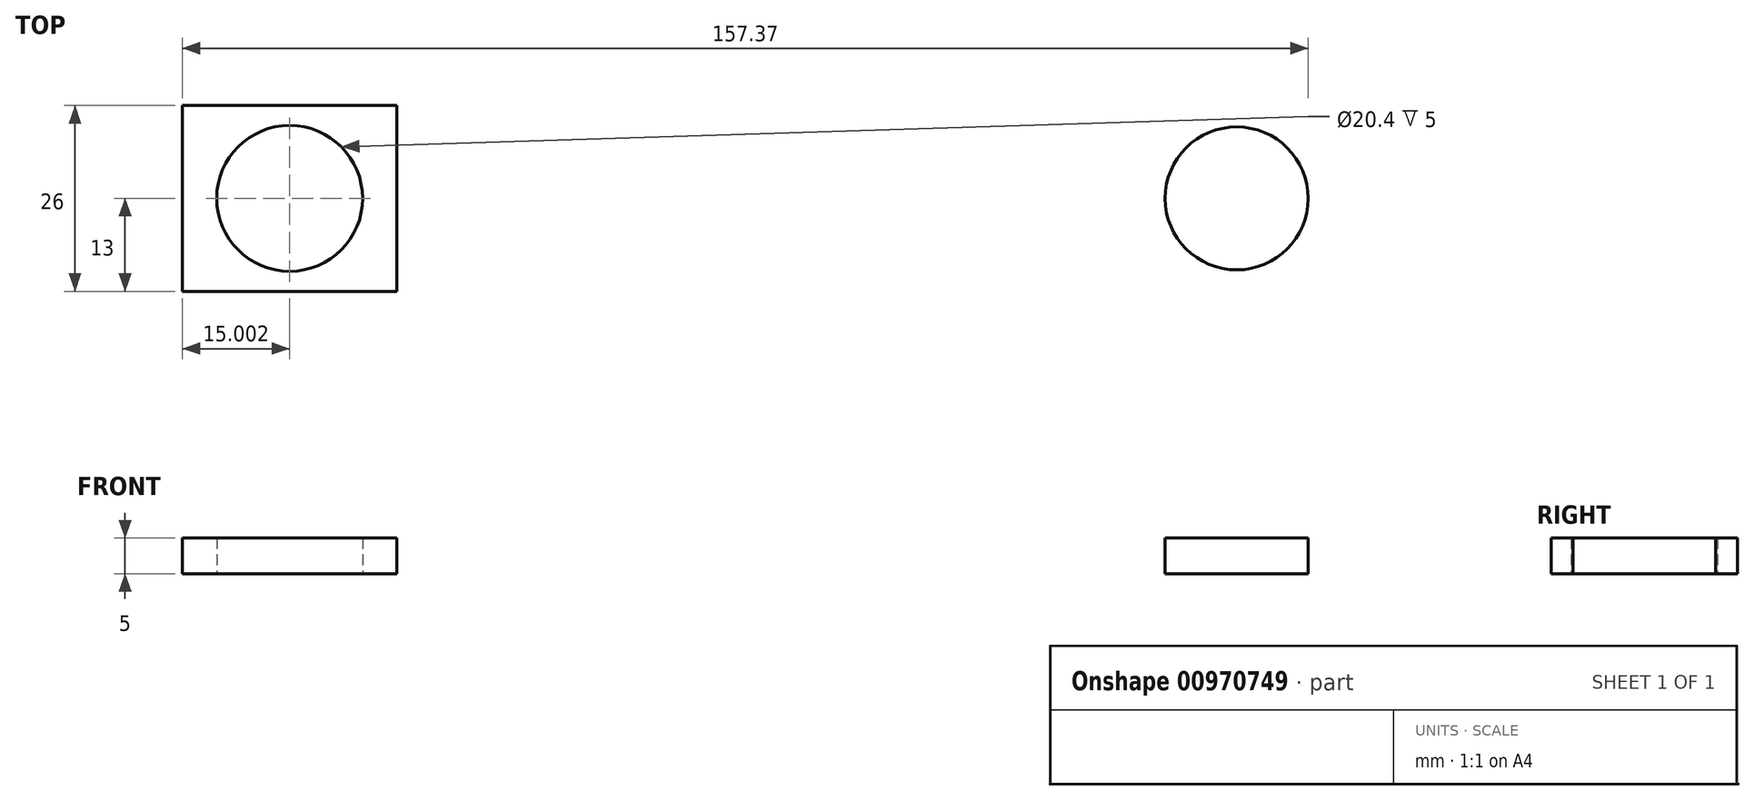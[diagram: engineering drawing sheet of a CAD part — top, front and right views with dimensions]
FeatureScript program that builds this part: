
annotation { "Feature Type Name" : "Feature", "Feature Type Description" : "" }
export const myFeature = defineFeature(function(context is Context, id is Id, definition is map)
    precondition{}
    {
        {
            var Q0;
            Q0=qCreatedBy(makeId("Top.planeOp"),FACE);
            var sketch = newSketch(context, id + "F0", { "sketchPlane" : qUnion([Q0])});
            skLineSegment(sketch, "E0", {"start": v(-147.37, -13) * mm, "end": v(-147.37, 13) * mm});
            skPoint(sketch, "E1.centerSnap0", {"position": v(-147.37, 0) * mm});
            skPoint(sketch, "E2", {"position": v(-143.37, 9) * mm});
            skPoint(sketch, "E3", {"position": v(-143.37, -9) * mm});
            skLineSegment(sketch, "E4", {"start": v(-117.37, 13) * mm, "end": v(-117.37, -13) * mm});
            skCircle(sketch, "E5", {"center": v(-132.37, 0) * mm, "radius": 10.2 * mm});
            skLineSegment(sketch, "E6", {"start": v(-147.37, 13) * mm, "end": v(-117.37, 13) * mm});
            skLineSegment(sketch, "E7", {"start": v(-147.37, -13) * mm, "end": v(-117.37, -13) * mm});
            skPoint(sketch, "E8", {"position": v(-121.37, 9) * mm});
            skPoint(sketch, "E9", {"position": v(-121.37, -9) * mm});
            skCircle(sketch, "E10", {"center": v(0, 0) * mm, "radius": 10 * mm});
            skSolve(sketch);
        }
        {
            var Q0;
            Q0=makeQuery(id+"F0.imprint","IMPRINT",FACE,{"disambiguationData":[TD([[makeQuery(id+"F0.imprint","IMPRINT",EDGE,{"derivedFrom":sQuery(id+"F0.wireOp",EDGE,"E0")}),-1.0]])]});
            var Q1;
            Q1=makeQuery(id+"F0.imprint","IMPRINT",FACE,{"disambiguationData":[TD([[makeQuery(id+"F0.imprint","IMPRINT",EDGE,{"derivedFrom":sQuery(id+"F0.wireOp",EDGE,"E10")}),1.0]])]});
            extrude(context, id + "F1", {"entities" : qUnion([Q0, Q1]), "depth" : 5 * mm, "offsetDistance" : 25 * mm});
        }
    });
